# Revit family: CVDDamper
name_source: partatom
category: Duct Accessories
revit_build: Autodesk Revit 2015 (Build: 20140606_1530(x64)
units: mm (PartAtom-declared; Revit-internal decimal feet)

## types (4) — shared parameters
Description = Constant Volume Damper
Electrical Phase = 1
Fax Number = +44(0)2920-858-222
Manufacturer = Nuaire
Manufacturer Name = Nuaire
Maximum Ambient Temperature = 40 °C
Number of Connection Poles = 2
Postcode = CF83 1NA
Revit Family Last Revised = 30/10/18
Telephone Number = +44(0)2920-858-200
URL = http://www.nuaire.co.uk
Unit Description = Constant Volume Damper
VAT Registration Number = 877308
Voltage = 230 V
Warranty Period = 3 Years
Weatherproof or Internal Only = Internal

## per-type parameters (varying)
| type | CVD100 | Classification.Uniclass.Pr.Description | Classification.Uniclass.Pr.Number | Height | ID | IFCExportAs | Length | OmniClass Number | OmniClass Title | Spigot Diameter | Spigot Radius | Weight | Width |
| CVD100 | Yes | Fans | Pr_65_67_29 | 160 mm  [stored 0.524934 ft] | 95 mm | IfcFanType | 201 mm  [stored 0.659449 ft] | 23-33 31 19 | Fans | 100 mm  [stored 0.328084 ft] | 50 mm  [stored 0.164042 ft] | 2.00 kg | 127 mm |
| CVD200 | No |  |  | 275 mm | 195 mm  [stored 0.639764 ft] |  | 300 mm |  |  | 200 mm  [stored 0.656168 ft] | 100 mm  [stored 0.328084 ft] | 4.00 kg | 230 mm  [stored 0.754593 ft] |
| CVD125 | No |  |  | 195 mm  [stored 0.639764 ft] | 120 mm |  | 300 mm |  |  | 125 mm  [stored 0.410105 ft] | 63 mm | 3.50 kg | 180 mm  [stored 0.590551 ft] |
| CVD150 | No |  |  | 220 mm  [stored 0.721785 ft] | 145 mm |  | 300 mm |  |  | 150 mm | 75 mm | 3.70 kg | 200 mm  [stored 0.656168 ft] |

note: column(s) folded — value = type name in every type: Model, Nuaire Model Code

note: [stored X ft] marks values corroborated as IEEE doubles in the binary element streams (Revit-internal decimal feet)

## geometry (parser evidence)
native form markers: Blend x8, Sweep x12
no freeform markers — native parametric forms only
